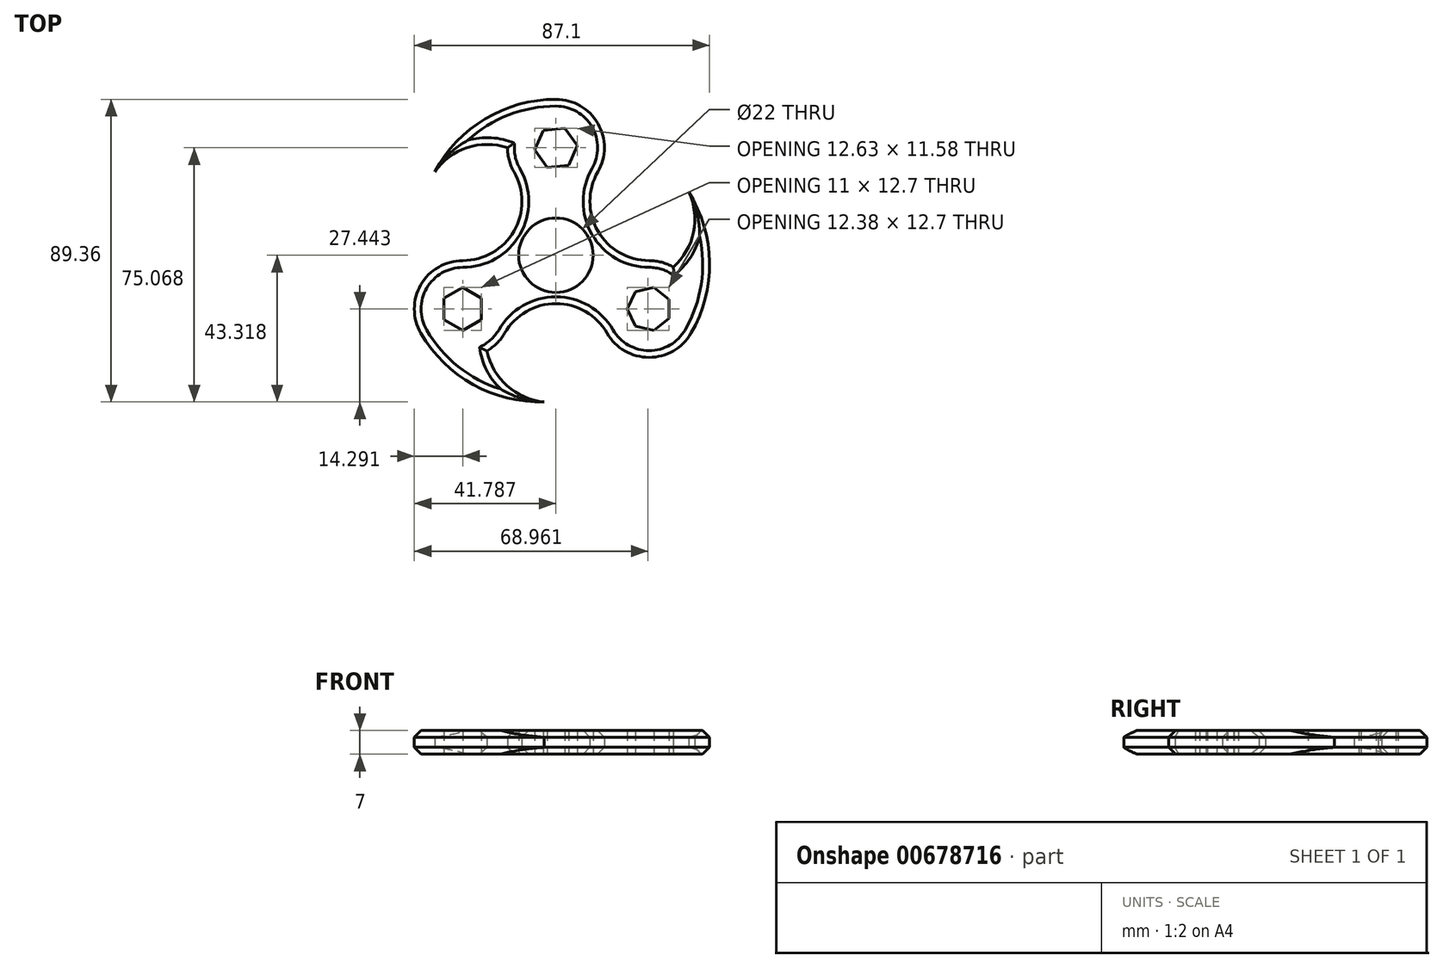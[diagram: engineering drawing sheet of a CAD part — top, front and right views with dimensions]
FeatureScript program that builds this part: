
annotation { "Feature Type Name" : "Feature", "Feature Type Description" : "" }
export const myFeature = defineFeature(function(context is Context, id is Id, definition is map)
    precondition{}
    {
        {
            var Q0;
            Q0=qCreatedBy(makeId("Top.planeOp"),FACE);
            var sketch = newSketch(context, id + "F0", { "sketchPlane" : qUnion([Q0])});
            skArc(sketch, "E0", {"start": v(-15.28, 32.26) * mm, "mid": v(-14.8, 28.56) * mm, "end": v(-13.37, 25.11) * mm});
            skCircle(sketch, "E1", {"center": v(-1, 0.5) * mm, "radius": 11 * mm});
            skArc(sketch, "E2.1.1", {"start": v(-28.49, -1.08) * mm, "mid": v(-40.86, -8.22) * mm, "end": v(-40.86, -22.51) * mm});
            skArc(sketch, "E2.2.1", {"start": v(14.13, -22.51) * mm, "mid": v(26.5, -29.65) * mm, "end": v(38.88, -22.51) * mm});
            skArc(sketch, "E3", {"start": v(-28.49, -1.08) * mm, "mid": v(-13.37, 7.65) * mm, "end": v(-13.37, 25.11) * mm});
            skArc(sketch, "E4.1.0", {"start": v(14.13, -22.51) * mm, "mid": v(-1, -13.78) * mm, "end": v(-16.12, -22.51) * mm});
            skArc(sketch, "E4.2.0", {"start": v(11.38, 25.11) * mm, "mid": v(11.38, 7.65) * mm, "end": v(26.5, -1.08) * mm});
            skArc(sketch, "E5", {"start": v(-1, 46.55) * mm, "mid": v(-21.85, 40.78) * mm, "end": v(-36.78, 25.11) * mm});
            skArc(sketch, "E6", {"start": v(-15.28, 32.26) * mm, "mid": v(-27.22, 32.26) * mm, "end": v(-36.78, 25.11) * mm});
            skPoint(sketch, "E7.center", {"position": v(-2.8, -1.16) * mm});
            skPoint(sketch, "E8.center", {"position": v(0.38, 21.82) * mm});
            skCircle(sketch, "E9.cCircle", {"center": v(26.5, -15.37) * mm, "radius": 5.87 * mm, "construction": true});
            skLineSegment(sketch, "E9.0", {"start": v(32.37, -12.54) * mm, "end": v(32.37, -18.2) * mm});
            skLineSegment(sketch, "E9.1", {"start": v(32.37, -18.2) * mm, "end": v(27.95, -21.72) * mm});
            skLineSegment(sketch, "E9.2", {"start": v(27.95, -21.72) * mm, "end": v(22.44, -20.46) * mm});
            skLineSegment(sketch, "E9.3", {"start": v(22.44, -20.46) * mm, "end": v(20, -15.37) * mm});
            skLineSegment(sketch, "E9.4", {"start": v(20, -15.37) * mm, "end": v(22.44, -10.27) * mm});
            skLineSegment(sketch, "E9.5", {"start": v(22.44, -10.27) * mm, "end": v(27.95, -9.02) * mm});
            skLineSegment(sketch, "E9.6", {"start": v(27.95, -9.02) * mm, "end": v(32.37, -12.54) * mm});
            skPoint(sketch, "E9.0.midPoint", {"position": v(32.37, -15.37) * mm});
            skCircle(sketch, "E10.cCircle", {"center": v(-28.49, -15.37) * mm, "radius": 5.5 * mm, "construction": true});
            skLineSegment(sketch, "E10.0", {"start": v(-33.99, -18.54) * mm, "end": v(-33.99, -12.2) * mm});
            skLineSegment(sketch, "E10.1", {"start": v(-33.99, -12.2) * mm, "end": v(-28.49, -9.02) * mm});
            skLineSegment(sketch, "E10.2", {"start": v(-28.49, -9.02) * mm, "end": v(-22.99, -12.2) * mm});
            skLineSegment(sketch, "E10.3", {"start": v(-22.99, -12.2) * mm, "end": v(-22.99, -18.54) * mm});
            skLineSegment(sketch, "E10.4", {"start": v(-22.99, -18.54) * mm, "end": v(-28.49, -21.72) * mm});
            skLineSegment(sketch, "E10.5", {"start": v(-28.49, -21.72) * mm, "end": v(-33.99, -18.54) * mm});
            skPoint(sketch, "E10.0.midPoint", {"position": v(-33.99, -15.37) * mm});
            skCircle(sketch, "E11.cCircle", {"center": v(-1, 32.26) * mm, "radius": 5.5 * mm, "construction": true});
            skLineSegment(sketch, "E11.0", {"start": v(2.72, 27.1) * mm, "end": v(-3.6, 26.47) * mm});
            skLineSegment(sketch, "E11.1", {"start": v(-3.6, 26.47) * mm, "end": v(-7.31, 31.62) * mm});
            skLineSegment(sketch, "E11.2", {"start": v(-7.31, 31.62) * mm, "end": v(-4.7, 37.4) * mm});
            skLineSegment(sketch, "E11.3", {"start": v(-4.7, 37.4) * mm, "end": v(1.61, 38.05) * mm});
            skLineSegment(sketch, "E11.4", {"start": v(1.61, 38.05) * mm, "end": v(5.32, 32.9) * mm});
            skLineSegment(sketch, "E11.5", {"start": v(5.32, 32.9) * mm, "end": v(2.72, 27.1) * mm});
            skPoint(sketch, "E11.0.midPoint", {"position": v(-0.44, 26.79) * mm});
            skArc(sketch, "E12.trimOffspring", {"start": v(-5.15, 28.62) * mm, "mid": v(-5.13, 28.61) * mm, "end": v(-5.1, 28.6) * mm});
            skPoint(sketch, "E13.orphan", {"position": v(-8.57, -43.72) * mm});
            skPoint(sketch, "E7.2.0.start.orphan", {"position": v(32.37, -7.07) * mm});
            skArc(sketch, "E14.1.0", {"start": v(-40.86, -22.51) * mm, "mid": v(-25.44, -37.69) * mm, "end": v(-4.4, -42.79) * mm});
            skArc(sketch, "E14.1.1", {"start": v(-21.35, -27.74) * mm, "mid": v(-15.38, -38.08) * mm, "end": v(-4.4, -42.79) * mm});
            skArc(sketch, "E14.2.0", {"start": v(38.88, -22.51) * mm, "mid": v(44.31, -1.56) * mm, "end": v(38.21, 19.2) * mm});
            skArc(sketch, "E14.2.1", {"start": v(33.65, -3) * mm, "mid": v(39.62, 7.34) * mm, "end": v(38.21, 19.2) * mm});
            skArc(sketch, "E15.trimOffspring", {"start": v(33.65, -3) * mm, "mid": v(30.2, -1.57) * mm, "end": v(26.5, -1.08) * mm});
            skArc(sketch, "E16.trimOffspring", {"start": v(-21.35, -27.74) * mm, "mid": v(-18.39, -25.47) * mm, "end": v(-16.12, -22.51) * mm});
            skArc(sketch, "E17.trimOffspring", {"start": v(11.38, 25.11) * mm, "mid": v(11.38, 39.4) * mm, "end": v(-1, 46.55) * mm});
            skSolve(sketch);
        }
        {
            var Q0;
            {var subQ0=sQuery(id+"F0.wireOp",EDGE,"E3");var subQ1=sQuery(id+"F0.wireOp",EDGE,"5f98a613-be39-42ef-9383-773c30fd98d7");var subQ2=makeQuery(id+"F0.imprint","INTERSECT",VERTEX,{"derivedFrom":[subQ1,subQ0]});Q0=makeQuery(id+"F0.imprint","IMPRINT",FACE,{"disambiguationData":[TD([[makeQuery(id+"F0.imprint","IMPRINT",EDGE,{"disambiguationData":[TD([[subQ2,-1.0]])],"derivedFrom":subQ1}),-1.0]])]});}
            var Q1;
            Q1=makeQuery(id+"F0.imprint","IMPRINT",FACE,{"disambiguationData":[TD([[makeQuery(id+"F0.imprint","IMPRINT",EDGE,{"derivedFrom":sQuery(id+"F0.wireOp",EDGE,"E2.1.0")}),-1.0]])]});
            var Q2;
            Q2=makeQuery(id+"F0.imprint","IMPRINT",FACE,{"disambiguationData":[TD([[makeQuery(id+"F0.imprint","IMPRINT",EDGE,{"derivedFrom":sQuery(id+"F0.wireOp",EDGE,"E2.1.0")}),1.0]])]});
            var Q3;
            {var subQ0=sQuery(id+"F0.wireOp",EDGE,"E14.1.0");Q3=makeQuery(id+"F0.imprint","IMPRINT",FACE,{"disambiguationData":[TD([[makeQuery(id+"F0.imprint","IMPRINT",EDGE,{"derivedFrom":subQ0}),1.0]])]});}
            var Q4;
            Q4=makeQuery(id+"F0.imprint","IMPRINT",FACE,{"disambiguationData":[TD([[makeQuery(id+"F0.imprint","IMPRINT",EDGE,{"derivedFrom":sQuery(id+"F0.wireOp",EDGE,"E1")}),-1.0]])]});
            var Q5;
            {var subQ0=sQuery(id+"F0.wireOp",EDGE,"E3");var subQ1=sQuery(id+"F0.wireOp",EDGE,"E0");var subQ2=makeQuery(id+"F0.imprint","INTERSECT",VERTEX,{"derivedFrom":[subQ1,subQ0]});Q5=makeQuery(id+"F0.imprint","IMPRINT",FACE,{"disambiguationData":[TD([[makeQuery(id+"F0.imprint","IMPRINT",EDGE,{"disambiguationData":[TD([[subQ2,-1.0]])],"derivedFrom":subQ1}),-1.0]])]});}
            var Q6;
            Q6=makeQuery(id+"F0.imprint","IMPRINT",FACE,{"disambiguationData":[TD([[makeQuery(id+"F0.imprint","IMPRINT",EDGE,{"derivedFrom":sQuery(id+"F0.wireOp",EDGE,"5811632c-25c7-4a81-935f-b205cc13fb21")}),-1.0]])]});
            var Q7;
            Q7=makeQuery(id+"F0.imprint","IMPRINT",FACE,{"disambiguationData":[TD([[makeQuery(id+"F0.imprint","IMPRINT",EDGE,{"derivedFrom":sQuery(id+"F0.wireOp",EDGE,"5811632c-25c7-4a81-935f-b205cc13fb21")}),1.0]])]});
            var Q8;
            {var subQ0=sQuery(id+"F0.wireOp",EDGE,"E5");Q8=makeQuery(id+"F0.imprint","IMPRINT",FACE,{"disambiguationData":[TD([[makeQuery(id+"F0.imprint","IMPRINT",EDGE,{"derivedFrom":subQ0}),1.0]])]});}
            var Q9;
            {var subQ0=sQuery(id+"F0.wireOp",EDGE,"E4.2.0");var subQ1=sQuery(id+"F0.wireOp",EDGE,"5f98a613-be39-42ef-9383-773c30fd98d7");var subQ2=makeQuery(id+"F0.imprint","INTERSECT",VERTEX,{"derivedFrom":[subQ1,subQ0]});Q9=makeQuery(id+"F0.imprint","IMPRINT",FACE,{"disambiguationData":[TD([[makeQuery(id+"F0.imprint","IMPRINT",EDGE,{"disambiguationData":[TD([[subQ2,1.0]])],"derivedFrom":subQ1}),-1.0]])]});}
            var Q10;
            Q10=makeQuery(id+"F0.imprint","IMPRINT",FACE,{"disambiguationData":[TD([[makeQuery(id+"F0.imprint","IMPRINT",EDGE,{"derivedFrom":sQuery(id+"F0.wireOp",EDGE,"E2.2.0")}),-1.0]])]});
            var Q11;
            Q11=makeQuery(id+"F0.imprint","IMPRINT",FACE,{"disambiguationData":[TD([[makeQuery(id+"F0.imprint","IMPRINT",EDGE,{"derivedFrom":sQuery(id+"F0.wireOp",EDGE,"E2.2.0")}),1.0]])]});
            var Q12;
            {var subQ0=sQuery(id+"F0.wireOp",EDGE,"E14.2.0");Q12=makeQuery(id+"F0.imprint","IMPRINT",FACE,{"disambiguationData":[TD([[makeQuery(id+"F0.imprint","IMPRINT",EDGE,{"derivedFrom":subQ0}),1.0]])]});}
            extrude(context, id + "F1", {"entities" : qUnion([Q0, Q1, Q2, Q3, Q4, Q5, Q6, Q7, Q8, Q9, Q10, Q11, Q12]), "depth" : 3.5 * mm, "offsetDistance" : 25.4 * mm, "hasSecondDirection" : true, "secondDirectionOppositeDirection" : true, "secondDirectionDepth" : 3.5 * mm});
        }
        {
            var Q0;
            Q0=makeQuery(id+"F1.opExtrude","CAP_EDGE",EDGE,{"disambiguationData":[OSD([sQuery(id+"F0.wireOp",EDGE,"E14.1.0")])],"isStart":false});
            var Q1;
            Q1=makeQuery(id+"F1.opExtrude","CAP_EDGE",EDGE,{"disambiguationData":[OSD([sQuery(id+"F0.wireOp",EDGE,"E14.1.0")])],"isStart":true});
            var Q2;
            Q2=makeQuery(id+"F1.opExtrude","CAP_EDGE",EDGE,{"disambiguationData":[OSD([sQuery(id+"F0.wireOp",EDGE,"E5")])],"isStart":true});
            var Q3;
            Q3=makeQuery(id+"F1.opExtrude","CAP_EDGE",EDGE,{"disambiguationData":[OSD([sQuery(id+"F0.wireOp",EDGE,"E5")])],"isStart":false});
            var Q4;
            Q4=makeQuery(id+"F1.opExtrude","CAP_EDGE",EDGE,{"disambiguationData":[OSD([sQuery(id+"F0.wireOp",EDGE,"E2.2.1")])],"isStart":true});
            var Q5;
            Q5=makeQuery(id+"F1.opExtrude","CAP_EDGE",EDGE,{"disambiguationData":[OSD([sQuery(id+"F0.wireOp",EDGE,"E2.2.1")])],"isStart":false});
            var Q6;
            Q6=makeQuery(id+"F1.opExtrude","CAP_EDGE",EDGE,{"disambiguationData":[OSD([sQuery(id+"F0.wireOp",EDGE,"E6")])],"isStart":false});
            var Q7;
            Q7=makeQuery(id+"F1.opExtrude","CAP_EDGE",EDGE,{"disambiguationData":[OSD([sQuery(id+"F0.wireOp",EDGE,"E14.2.1")])],"isStart":true});
            var Q8;
            Q8=makeQuery(id+"F1.opExtrude","CAP_EDGE",EDGE,{"disambiguationData":[OSD([sQuery(id+"F0.wireOp",EDGE,"E14.2.1")])],"isStart":false});
            var Q9;
            Q9=makeQuery(id+"F1.opExtrude","CAP_EDGE",EDGE,{"disambiguationData":[OSD([sQuery(id+"F0.wireOp",EDGE,"E6")])],"isStart":true});
            var Q10;
            Q10=makeQuery(id+"F1.opExtrude","CAP_EDGE",EDGE,{"disambiguationData":[OSD([sQuery(id+"F0.wireOp",EDGE,"E14.1.1")])],"isStart":true});
            var Q11;
            Q11=makeQuery(id+"F1.opExtrude","CAP_EDGE",EDGE,{"disambiguationData":[OSD([sQuery(id+"F0.wireOp",EDGE,"E14.1.1")])],"isStart":false});
            chamfer(context, id + "F2", {"entities" : qUnion([Q0, Q1, Q2, Q3, Q4, Q5, Q6, Q7, Q8, Q9, Q10, Q11]), "width" : 2 * mm, "tangentPropagation" : true});
        }
    });
